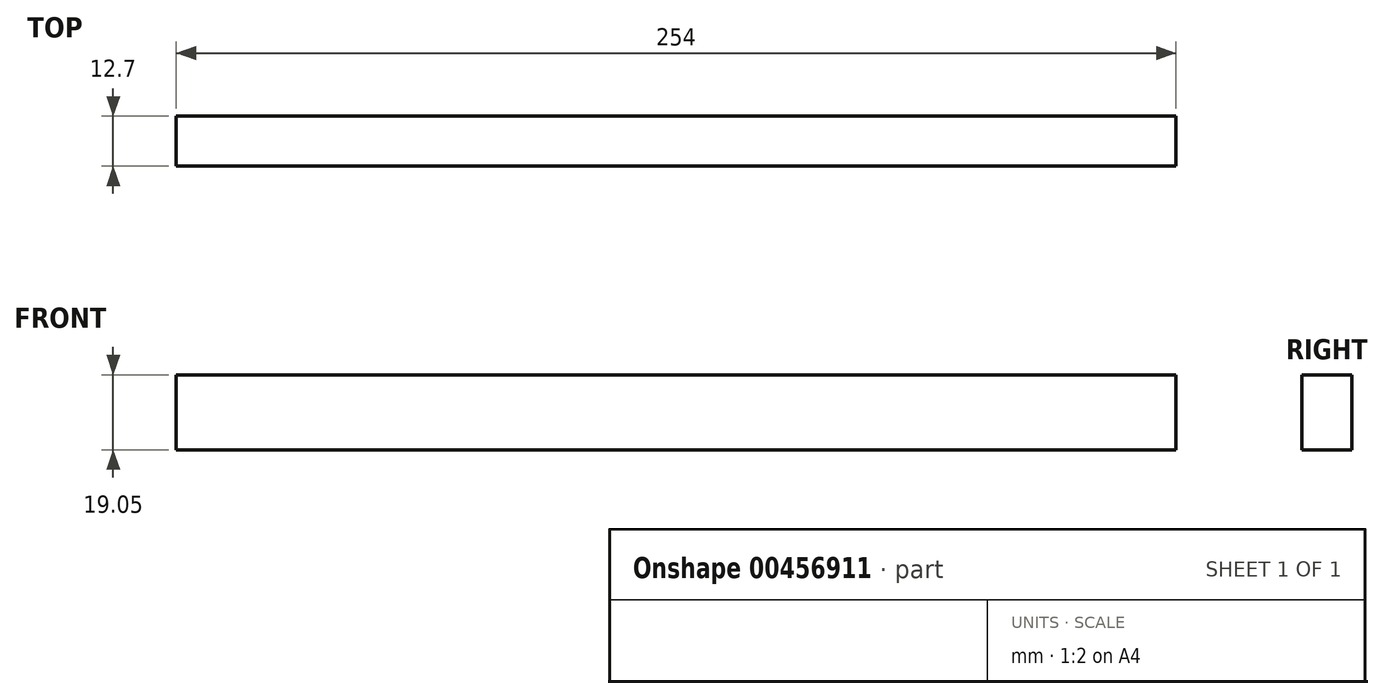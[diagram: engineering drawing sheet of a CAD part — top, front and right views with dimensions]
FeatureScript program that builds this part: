
annotation { "Feature Type Name" : "Feature", "Feature Type Description" : "" }
export const myFeature = defineFeature(function(context is Context, id is Id, definition is map)
    precondition{}
    {
        {
            var Q0;
            Q0=qCreatedBy(makeId("Front.planeOp"),FACE);
            var sketch = newSketch(context, id + "F0", { "sketchPlane" : qUnion([Q0])});
            skLineSegment(sketch, "E0.bottom", {"start": v(193.04, 154.51) * mm, "end": v(193.04, 135.46) * mm});
            skLineSegment(sketch, "E0.top", {"start": v(-60.96, 154.51) * mm, "end": v(-60.96, 135.46) * mm});
            skLineSegment(sketch, "E0.left", {"start": v(193.04, 154.51) * mm, "end": v(-60.96, 154.51) * mm});
            skLineSegment(sketch, "E0.right", {"start": v(193.04, 135.46) * mm, "end": v(-60.96, 135.46) * mm});
            skSolve(sketch);
        }
        {
            var Q0;
            Q0=makeQuery(id+"F0.imprint","IMPRINT",FACE,{"disambiguationData":[TD([[makeQuery(id+"F0.imprint","IMPRINT",EDGE,{"derivedFrom":sQuery(id+"F0.wireOp",EDGE,"CR0fLDGC-FUSB-T87a-WjLq-PKh2d8LQHOZw.bottom")}),-1.0]])]});
            var Q1;
            Q1=makeQuery(id+"F0.imprint","IMPRINT",FACE,{"disambiguationData":[TD([[makeQuery(id+"F0.imprint","IMPRINT",EDGE,{"derivedFrom":sQuery(id+"F0.wireOp",EDGE,"E0.bottom")}),-1.0]])]});
            extrude(context, id + "F1", {"entities" : qUnion([Q0, Q1]), "depth" : 12.7 * mm});
        }
    });
